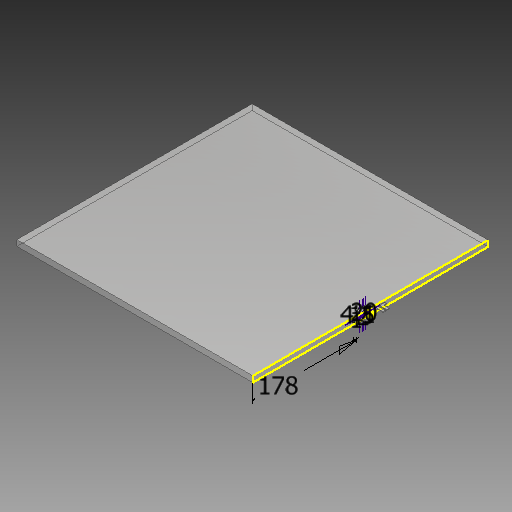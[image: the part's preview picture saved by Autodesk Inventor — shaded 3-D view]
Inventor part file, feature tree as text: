
AUTODESK INVENTOR PART (.ipt)
format: ipt  version: 2018.2 (Build 222227000, 227)  size: 162,816 bytes
history: native  units: mm
features: extrude x3, sketch x2, pattern_linear x1, projected_geometry x1
ambient origin geometry x8: Origin, YZ Plane, XZ Plane, XY Plane, X Axis, Y Axis, Z Axis, Center Point
bodies: Volumenkörper1 (feature_tree)
feature tree (7):
  extrude  "Extrusion1"  Depth=400.0mm
  sketch  "Skizze2"  dims[d2=10.0mm d3=0.0mm d4=20.0mm d5=1.0mm d6=11.0mm d7=2.0mm d8=4.5mm d10=178.0mm d11=4.0mm d12=0.0mm d15=13.0mm d16=0.0mm d17=20.0mm d19=27.0mm]
  extrude  "Extrusion2"  Depth=20.0mm
  extrude  "Extrusion4"  Depth=1.0mm
  pattern_linear  "Rechteckige Anordnung1"  Spacing1=11.0mm  [1 undecoded]
  sketch  "Skizze1"  dims[d0=400.0mm d1=400.0mm]
  projected_geometry  "Projizierte Kontur1"
note: 1 required parameter value undecoded (feature->parameter linkage not recoverable at this tier; creation-order binding heuristic only, values carry confidence <= 0.55)
